FREECAD ASSEMBLY — COMPONENT RECIPES ("K93-10436-H7-L120_reference_PJ-063AH_slot1_up")

This assembly document has 3 components, labeled P0..P2 below (a component is one placed body or linked part). 0 of them carry a construction recipe — the FreeCAD feature program that regenerates the part from scratch, quoted from this document or its linked companion documents; the rest are supplied as boundary geometry only. No exploded tour is included for this assembly.
COMPONENT P0 — geometry summary ("K93-10436-H7-L120_frontpanel_PJ-063AH_slot1_up"; no construction recipe available for this part):
  bounding box: 104.0 x 36.0 x 1.5 mm
  tessellated surface: 6,084 triangles
  volume: 5350 mm^3 (95% of its bounding box)
COMPONENT P1 — geometry summary ("K93-120"; no construction recipe available for this part):
  bounding box: 121.5 x 104.0 x 36.0 mm
  tessellated surface: 10,556 triangles
  volume: 84663 mm^3 (19% of its bounding box)
  symmetry: 2-fold rotationally symmetric about the y axis
COMPONENT P2 — geometry summary ("Reference_PJ-063AH 1"; no construction recipe available for this part):
  bounding box: 119.6 x 99.6 x 14.7 mm
  tessellated surface: 24,828 triangles
  volume: 20538 mm^3 (12% of its bounding box)
PROVENANCE & LICENSES
A FreeCAD (.FCStd) document from a public repository crawl; recipes are the document's own serialized feature recipes (and, for linked parts, companion documents' recipes).
License: mit.
